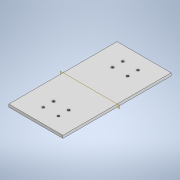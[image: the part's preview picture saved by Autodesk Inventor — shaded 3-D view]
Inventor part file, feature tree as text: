
AUTODESK INVENTOR PART (.ipt)
format: ipt  version: 2020 (Build 240168000, 168)  size: 126,976 bytes
history: native  units: in
note: dims shown in document units (in); Inventor stores cm internally (conversion verified against a paired STEP export)
features: sketch x3, hole x2, extrude x1, mirror x1
ambient origin geometry x8: Origin, YZ Plane, XZ Plane, XY Plane, X Axis, Y Axis, Z Axis, Center Point
bodies: Solid1 (feature_tree)
feature tree (7):
  extrude  "Extrusion1"  Depth=7.874in
  hole  "Hole1"  [1 undecoded]
  hole  "Hole2"  [1 undecoded]
  mirror  "Mirror2"
  sketch  "Sketch1"  dims[d0=3.937in d1=7.874in]
  sketch  "Sketch2"  dims[d2=0.1969in d3=0.0in d4=2.7244in]
  sketch  "Sketch3"  dims[d5=4.5669in d6=0.7677in d7=1.1024in d8=0.1378in d9=0.1378in d10=0.1969in d11=0.1969in d12=2.7559in d13=180.0deg d14=0.1755in d15=0.3937in d16=0.1575in d17=0.0787in d18=90.0deg d19=0.5039in d20=0.8108in d21=2.7244in d22=6.378in d23=0.2953in d24=0.2953in d25=1.1024in d26=0.7677in d27=0.1628in d28=0.3937in d29=0.1575in d30=0.0787in d31=90.0deg d32=0.315in d33=0.8108in]
note: 2 required parameter values undecoded (feature->parameter linkage not recoverable at this tier; creation-order binding heuristic only, values carry confidence <= 0.55)
